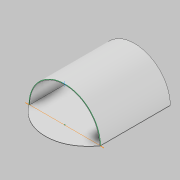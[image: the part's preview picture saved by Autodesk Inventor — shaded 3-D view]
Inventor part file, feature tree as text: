
AUTODESK INVENTOR PART (.ipt)
format: ipt  version: 2021 (Build 250183000, 183)  size: 340,480 bytes
history: native  units: in
note: dims shown in document units (in); Inventor stores cm internally (conversion verified against a paired STEP export)
features: sketch x7, other x5, extrude x3, plane x2
ambient origin geometry x8: Origin, YZ Plane, XZ Plane, XY Plane, X Axis, Y Axis, Z Axis, Center Point
bodies: Solid1 (feature_tree)
feature tree (17):
  extrude  "base"  Depth=49.2126in TaperAngle=0.0deg
  plane  "Work Plane2"
  sketch  "Sketch4"  dims[d7=10.4945in d8=2.5245in]
  plane  "Work Plane3"
  sketch  "Sketch5"  dims[d9=10.5827in]
  other  "Form3"
  sketch  "Sketch6"  dims[d10=0.1969in d11=0.0in]
  extrude  "Extrusion2"  TaperAngle=0.0deg  [1 undecoded]
  sketch  "Sketch10"  dims[d13=0.0in d14=0.3937in d15=0.3937in d18=23.622in d19=4.7268in d20=8.7975in d21=14.6427in d22=20.2443in d23=2.531in d24=5.1396in d25=10.1154in d26=17.5615in d27=27.7209in d28=14.6427in d29=6.2924in d30=6.2924in d31=12.4958in d32=12.4958in d33=19.685in d34=0.0in d35=0.0in d38=0.3937in]
  sketch  "Sketch1"  dims[d0=19.685in d1=49.2126in d2=0.0in]
  other  "Srf2"
  sketch  "Sketch3"  dims[d4=0.0in d5=0.0in]
  other  "Matched Edge1"
  other  "Matches"
  sketch  "Sketch7"  dims[d12=-7.874in]
  extrude  "ExtrusionSrf1"  Depth=2.5245in
  other  "Srf4"
note: 1 required parameter value undecoded (feature->parameter linkage not recoverable at this tier; creation-order binding heuristic only, values carry confidence <= 0.55)
